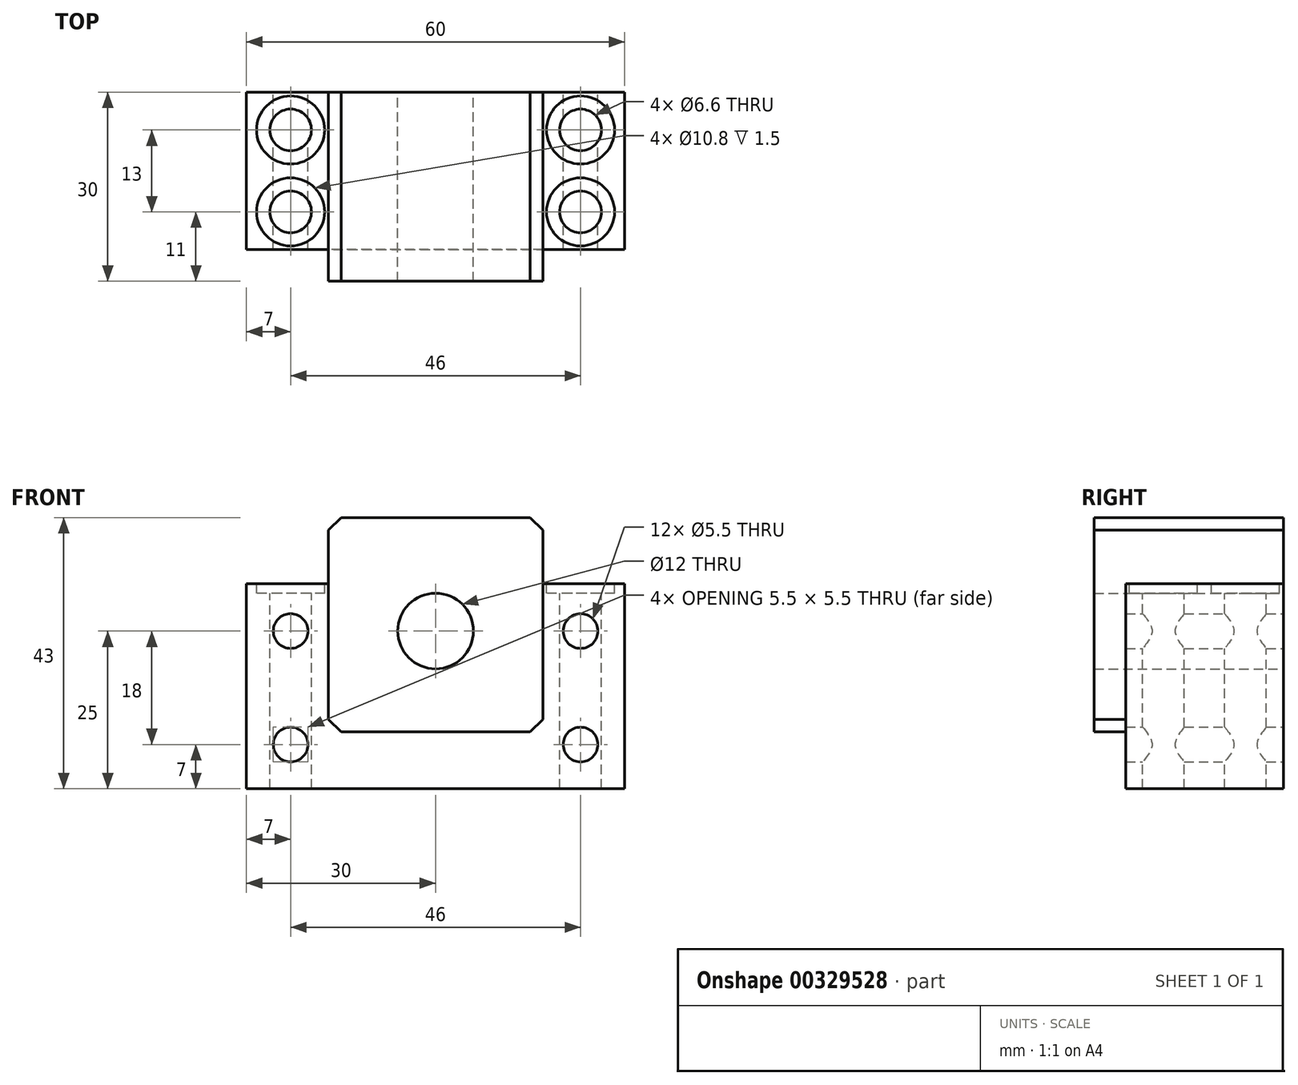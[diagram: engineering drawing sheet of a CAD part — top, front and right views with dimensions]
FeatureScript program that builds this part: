
annotation { "Feature Type Name" : "Feature", "Feature Type Description" : "" }
export const myFeature = defineFeature(function(context is Context, id is Id, definition is map)
    precondition{}
    {
        {
            var Q0;
            Q0=qCreatedBy(makeId("Front.planeOp"),FACE);
            var sketch = newSketch(context, id + "F0", { "sketchPlane" : qUnion([Q0])});
            skCircle(sketch, "E0", {"center": v(0, 0) * mm, "radius": 6 * mm});
            skLineSegment(sketch, "E1.bottom", {"start": v(-30, -25) * mm, "end": v(30, -25) * mm});
            skLineSegment(sketch, "E1.top", {"start": v(-30, 7.5) * mm, "end": v(-17, 7.5) * mm});
            skLineSegment(sketch, "E1.left", {"start": v(-30, -25) * mm, "end": v(-30, 7.5) * mm});
            skLineSegment(sketch, "E1.right", {"start": v(30, -25) * mm, "end": v(30, 7.5) * mm});
            skLineSegment(sketch, "E2.top", {"start": v(-15, 18) * mm, "end": v(15, 18) * mm});
            skLineSegment(sketch, "E2.left", {"start": v(-17, 7.5) * mm, "end": v(-17, 16) * mm});
            skLineSegment(sketch, "E2.right", {"start": v(17, 7.5) * mm, "end": v(17, 16) * mm});
            skLineSegment(sketch, "E3.trimOffspring", {"start": v(17, 7.5) * mm, "end": v(30, 7.5) * mm});
            skCircle(sketch, "E4", {"center": v(-23, 0) * mm, "radius": 2.75 * mm});
            skCircle(sketch, "E5", {"center": v(-23, -18) * mm, "radius": 2.75 * mm});
            skCircle(sketch, "E6", {"center": v(23, -18) * mm, "radius": 2.75 * mm});
            skCircle(sketch, "E7", {"center": v(23, 0) * mm, "radius": 2.75 * mm});
            skLineSegment(sketch, "E8", {"start": v(-15, 18) * mm, "end": v(-17, 16) * mm});
            skLineSegment(sketch, "E9", {"start": v(15, 18) * mm, "end": v(17, 16) * mm});
            skPoint(sketch, "E10.orphan", {"position": v(-17, 18) * mm});
            skPoint(sketch, "E11.orphan", {"position": v(17, 18) * mm});
            skSolve(sketch);
        }
        {
            var Q0;
            Q0 = qSketchRegion(id + "F0", true);
            extrude(context, id + "F1", {"entities" : qUnion([Q0]), "endBound" : BoundingType.SYMMETRIC, "depth" : 25 * mm});
        }
        {
            var Q0;
            Q0=makeQuery(id+"F1.opExtrude","CAP_FACE",FACE,{"disambiguationData":[OSD([sQuery(id+"F0.wireOp",EDGE,"E0"),sQuery(id+"F0.wireOp",EDGE,"E1.bottom"),sQuery(id+"F0.wireOp",EDGE,"E1.top"),sQuery(id+"F0.wireOp",EDGE,"E1.left"),sQuery(id+"F0.wireOp",EDGE,"E1.right"),sQuery(id+"F0.wireOp",EDGE,"E2.top"),sQuery(id+"F0.wireOp",EDGE,"E2.left"),sQuery(id+"F0.wireOp",EDGE,"E2.right"),sQuery(id+"F0.wireOp",EDGE,"E3.trimOffspring"),sQuery(id+"F0.wireOp",EDGE,"E4"),sQuery(id+"F0.wireOp",EDGE,"E5"),sQuery(id+"F0.wireOp",EDGE,"E6"),sQuery(id+"F0.wireOp",EDGE,"E7")])],"isStart":false});
            var sketch = newSketch(context, id + "F2", { "sketchPlane" : qUnion([Q0])});
            skLineSegment(sketch, "E12", {"start": v(-17, 16) * mm, "end": v(-15, 18) * mm});
            skLineSegment(sketch, "E13", {"start": v(-15, 18) * mm, "end": v(15, 18) * mm});
            skLineSegment(sketch, "E14", {"start": v(15, 18) * mm, "end": v(17, 16) * mm});
            skLineSegment(sketch, "E15", {"start": v(17, 16) * mm, "end": v(17, -14) * mm});
            skLineSegment(sketch, "E16", {"start": v(17, -14) * mm, "end": v(15, -16) * mm});
            skLineSegment(sketch, "E17", {"start": v(15, -16) * mm, "end": v(-15, -16) * mm});
            skLineSegment(sketch, "E18", {"start": v(-15, -16) * mm, "end": v(-17, -14) * mm});
            skLineSegment(sketch, "E19", {"start": v(-17, -14) * mm, "end": v(-17, 16) * mm});
            skCircle(sketch, "E20", {"center": v(0, 0) * mm, "radius": 6 * mm});
            skSolve(sketch);
        }
        {
            var Q0;
            Q0 = qSketchRegion(id + "F2", true);
            extrude(context, id + "F3", {"entities" : qUnion([Q0]), "operationType" : NewBodyOperationType.ADD, "depth" : 5 * mm});
        }
        {
            var Q0;
            Q0=makeQuery(id+"F1.opExtrude","SWEPT_FACE",FACE,{"disambiguationData":[OSD([sQuery(id+"F0.wireOp",EDGE,"E3.trimOffspring")])]});
            var sketch = newSketch(context, id + "F4", { "sketchPlane" : qUnion([Q0])});
            skPoint(sketch, "E21", {"position": v(-23, 6.5) * mm});
            skPoint(sketch, "E22", {"position": v(-23, -6.5) * mm});
            skPoint(sketch, "E23", {"position": v(23, 6.5) * mm});
            skPoint(sketch, "E24", {"position": v(23, -6.5) * mm});
            skSolve(sketch);
        }
        {
            var Q0;
            Q0=sQuery(id+"F4.wireOp",VERTEX,"E21");
            var Q1;
            Q1=sQuery(id+"F4.wireOp",VERTEX,"E22");
            var Q2;
            Q2=sQuery(id+"F4.wireOp",VERTEX,"E23");
            var Q3;
            Q3=sQuery(id+"F4.wireOp",VERTEX,"E24");
            var Q4;
            Q4=makeQuery(id+"F1.opExtrude","SWEPT_BODY",BODY,{"disambiguationData":[OSD([sQuery(id+"F0.wireOp",EDGE,"E0"),sQuery(id+"F0.wireOp",EDGE,"E1.bottom"),sQuery(id+"F0.wireOp",EDGE,"E1.top"),sQuery(id+"F0.wireOp",EDGE,"E1.left"),sQuery(id+"F0.wireOp",EDGE,"E1.right"),sQuery(id+"F0.wireOp",EDGE,"E2.top"),sQuery(id+"F0.wireOp",EDGE,"E2.left"),sQuery(id+"F0.wireOp",EDGE,"E2.right"),sQuery(id+"F0.wireOp",EDGE,"E3.trimOffspring"),sQuery(id+"F0.wireOp",EDGE,"E4"),sQuery(id+"F0.wireOp",EDGE,"E5"),sQuery(id+"F0.wireOp",EDGE,"E6"),sQuery(id+"F0.wireOp",EDGE,"E7")])]});
            hole(context, id + "F5", {"style" : HoleStyle.C_BORE, "endStyle" : HoleEndStyle.THROUGH, "holeDiameter" : 6.6 * mm, "cBoreDiameter" : 10.8 * mm, "cBoreDepth" : 1.5 * mm, "tappedDepth" : 9.6 * mm, "tapClearance" : 3, "locations" : qUnion([Q0, Q1, Q2, Q3]), "scope" : qUnion([Q4])});
        }
    });
